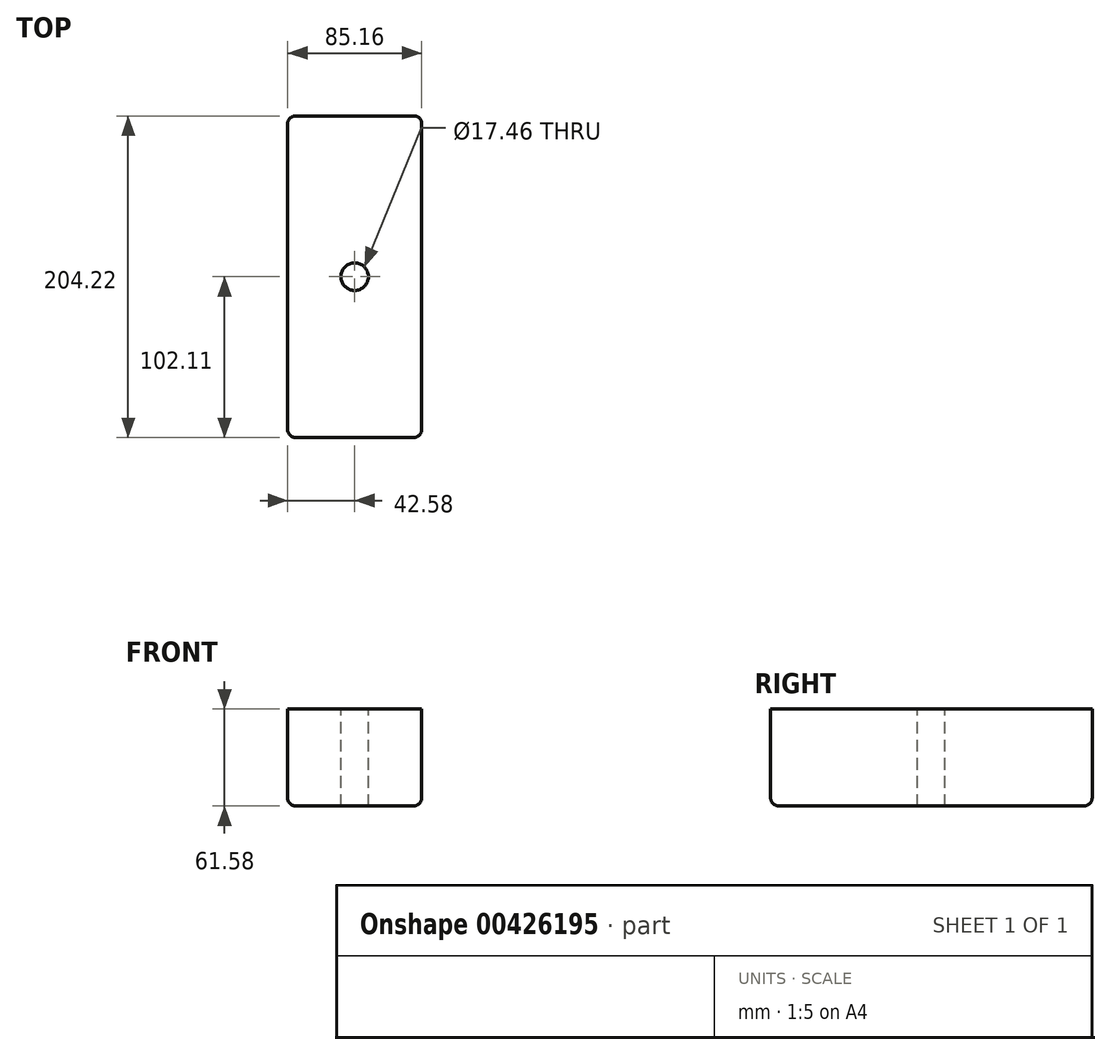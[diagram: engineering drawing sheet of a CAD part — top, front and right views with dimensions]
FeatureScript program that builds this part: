
annotation { "Feature Type Name" : "Feature", "Feature Type Description" : "" }
export const myFeature = defineFeature(function(context is Context, id is Id, definition is map)
    precondition{}
    {
        {
            var Q0;
            Q0=qCreatedBy(makeId("Front.planeOp"),FACE);
            var sketch = newSketch(context, id + "F0", { "sketchPlane" : qUnion([Q0])});
            skLineSegment(sketch, "E0.bottom", {"start": v(42.58, 30.8) * mm, "end": v(-42.58, 30.8) * mm});
            skLineSegment(sketch, "E0.top", {"start": v(42.58, -30.8) * mm, "end": v(-42.58, -30.8) * mm});
            skLineSegment(sketch, "E0.left", {"start": v(42.58, 30.8) * mm, "end": v(42.58, -30.8) * mm});
            skLineSegment(sketch, "E0.right", {"start": v(-42.58, 30.8) * mm, "end": v(-42.58, -30.8) * mm});
            skPoint(sketch, "E0.middle", {"position": v(0, 0) * mm});
            skSolve(sketch);
        }
        {
            var Q0;
            Q0=makeQuery(id+"F0.imprint","IMPRINT",FACE,{"disambiguationData":[TD([[makeQuery(id+"F0.imprint","IMPRINT",EDGE,{"derivedFrom":sQuery(id+"F0.wireOp",EDGE,"E0.bottom")}),1.0]])]});
            extrude(context, id + "F1", {"entities" : qUnion([Q0]), "endBound" : BoundingType.SYMMETRIC, "depth" : 204.22 * mm, "offsetDistance" : 25.4 * mm});
        }
        {
            var Q0;
            Q0=makeQuery(id+"F1.opExtrude","SWEPT_FACE",FACE,{"disambiguationData":[OSD([sQuery(id+"F0.wireOp",EDGE,"E0.bottom")])]});
            var sketch = newSketch(context, id + "F2", { "sketchPlane" : qUnion([Q0])});
            skPoint(sketch, "E1", {"position": v(0, 0) * mm});
            skSolve(sketch);
        }
        {
            var Q0;
            Q0=sQuery(id+"F2.wireOp",VERTEX,"E1");
            var Q1;
            Q1=makeQuery(id+"F1.opExtrude","SWEPT_BODY",BODY,{"disambiguationData":[OSD([sQuery(id+"F0.wireOp",EDGE,"E0.bottom"),sQuery(id+"F0.wireOp",EDGE,"E0.top"),sQuery(id+"F0.wireOp",EDGE,"E0.left"),sQuery(id+"F0.wireOp",EDGE,"E0.right")])]});
            hole(context, id + "F3", {"style" : HoleStyle.SIMPLE, "endStyle" : HoleEndStyle.THROUGH, "standardTappedOrClearance" : lookupTablePath({ "standard" : "ANSI", "engagement" : "75%", "pitch" : "16 tpi", "size" : "3/4", "type" : "Tapped" }), "standardBlindInLast" : lookupTablePath({ "standard" : "ANSI", "fit" : "Free", "engagement" : "75%", "pitch" : "16 tpi", "size" : "3/4", "type" : "Clearance & tapped" }), "holeDiameter" : 17.46 * mm, "majorDiameter" : 19.05 * mm, "showTappedDepth" : true, "isTappedThrough" : true, "tappedDepth" : 12.7 * mm, "tapClearance" : 3, "locations" : qUnion([Q0]), "scope" : qUnion([Q1])});
        }
        {
            var Q0;
            Q0=makeQuery(id+"F1.opExtrude","CAP_EDGE",EDGE,{"disambiguationData":[OSD([sQuery(id+"F0.wireOp",EDGE,"E0.top")])],"isStart":false});
            var Q1;
            Q1=makeQuery(id+"F1.opExtrude","SWEPT_EDGE",EDGE,{"disambiguationData":[OSD([sQuery(id+"F0.wireOp",EDGE,"E0.top"),sQuery(id+"F0.wireOp",EDGE,"E0.left")])]});
            var Q2;
            Q2=makeQuery(id+"F1.opExtrude","CAP_EDGE",EDGE,{"disambiguationData":[OSD([sQuery(id+"F0.wireOp",EDGE,"E0.top")])],"isStart":true});
            var Q3;
            Q3=makeQuery(id+"F1.opExtrude","SWEPT_EDGE",EDGE,{"disambiguationData":[OSD([sQuery(id+"F0.wireOp",EDGE,"E0.top"),sQuery(id+"F0.wireOp",EDGE,"E0.right")])]});
            var Q4;
            Q4=makeQuery(id+"F1.opExtrude","CAP_EDGE",EDGE,{"disambiguationData":[OSD([sQuery(id+"F0.wireOp",EDGE,"E0.right")])],"isStart":false});
            var Q5;
            Q5=makeQuery(id+"F1.opExtrude","CAP_EDGE",EDGE,{"disambiguationData":[OSD([sQuery(id+"F0.wireOp",EDGE,"E0.right")])],"isStart":true});
            var Q6;
            Q6=makeQuery(id+"F1.opExtrude","CAP_EDGE",EDGE,{"disambiguationData":[OSD([sQuery(id+"F0.wireOp",EDGE,"E0.left")])],"isStart":true});
            var Q7;
            Q7=makeQuery(id+"F1.opExtrude","CAP_EDGE",EDGE,{"disambiguationData":[OSD([sQuery(id+"F0.wireOp",EDGE,"E0.left")])],"isStart":false});
            fillet(context, id + "F4", {"entities" : qUnion([Q0, Q1, Q2, Q3, Q4, Q5, Q6, Q7]), "tangentPropagation" : true, "radius" : 5.08 * mm, "defaultsChanged" : false, "vertexSettings" : [], "allowEdgeOverflow" : false});
        }
    });
